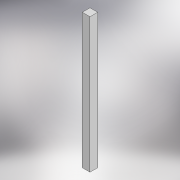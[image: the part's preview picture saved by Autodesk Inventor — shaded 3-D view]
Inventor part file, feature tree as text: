
AUTODESK INVENTOR PART (.ipt)
format: ipt  version: 2020 (Build 240168000, 168)  size: 105,472 bytes
history: native  units: mm
features: extrude x1, sketch x1
ambient origin geometry x8: Origin, YZ Plane, XZ Plane, XY Plane, X Axis, Y Axis, Z Axis, Center Point
bodies: Solid1 (feature_tree)
feature tree (2):
  extrude  "Extrusion1"  Depth=40.0mm
  sketch  "Sketch1"  dims[d0=40.0mm d1=40.0mm d2=700.0mm d3=0.0mm]
